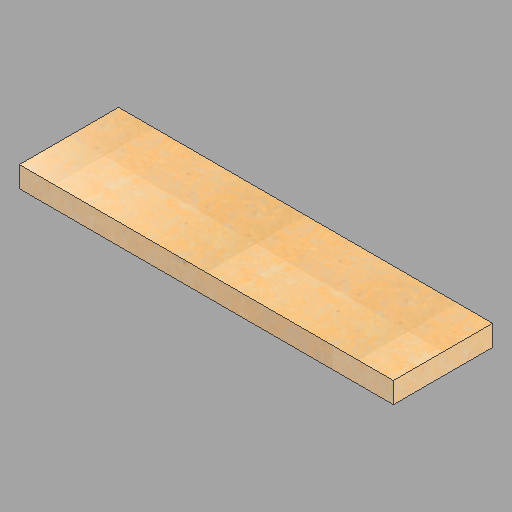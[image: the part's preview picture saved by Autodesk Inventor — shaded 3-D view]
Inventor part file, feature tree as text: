
AUTODESK INVENTOR PART (.ipt)
format: ipt  version: 2023 (Build 270158000, 158)  size: 210,432 bytes
history: native  units: in
note: dims shown in document units (in); Inventor stores cm internally (conversion verified against a paired STEP export)
features: extrude x1, sketch x1
ambient origin geometry x8: Origin, YZ Plane, XZ Plane, XY Plane, X Axis, Y Axis, Z Axis, Center Point
bodies: Solid1 (feature_tree)
feature tree (2):
  extrude  "Extrusion1"  Depth=19.0in
  sketch  "Sketch1"  dims[d0=71.625in d1=19.0in d2=4.0in d3=0.0in]
